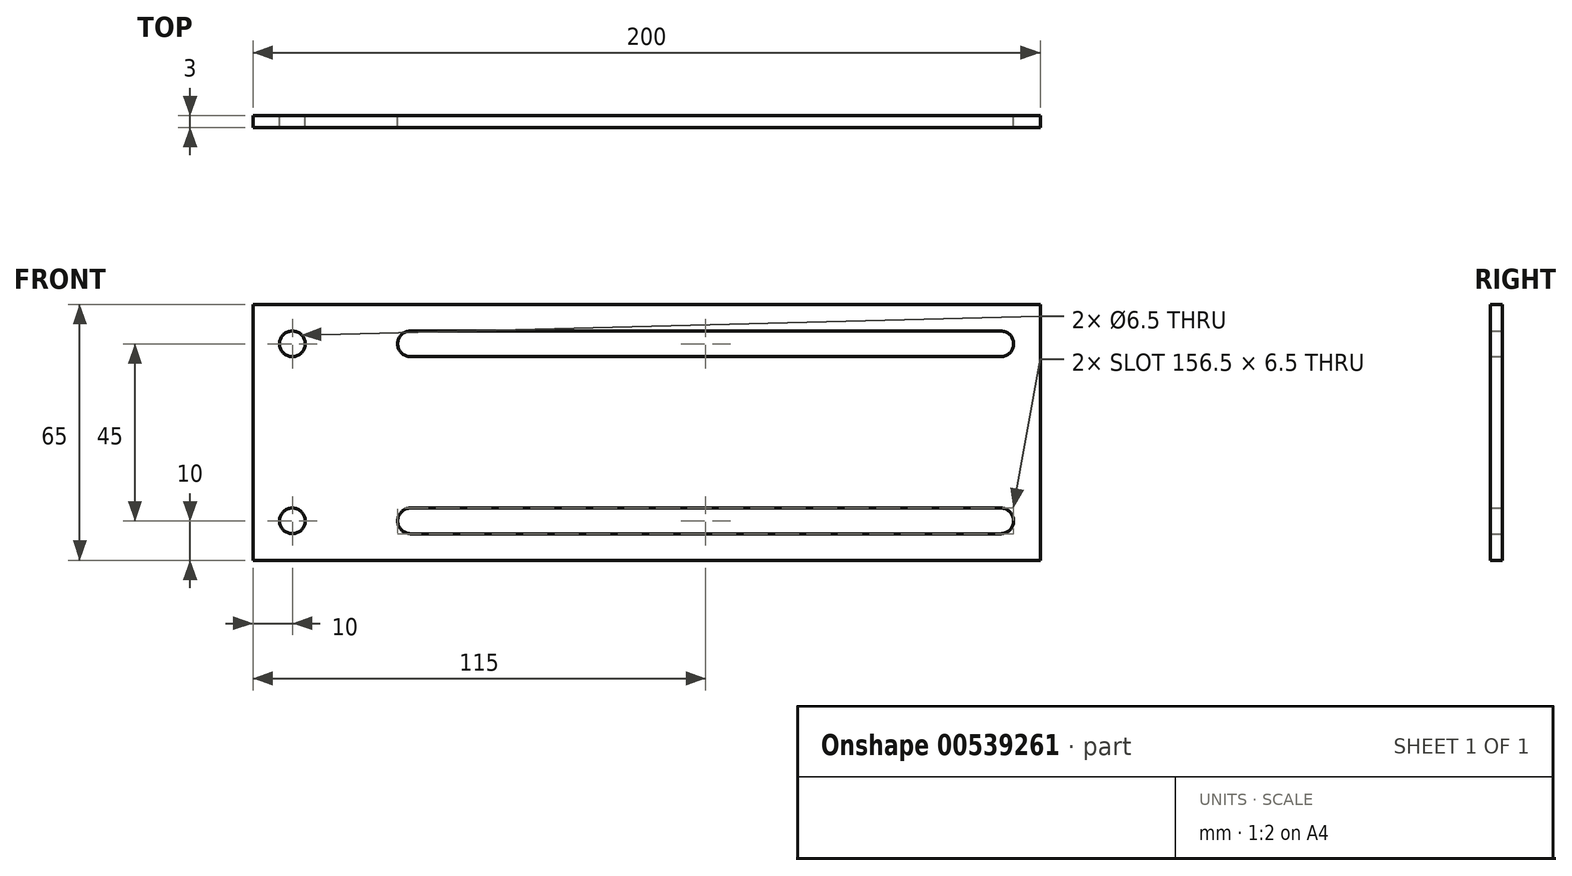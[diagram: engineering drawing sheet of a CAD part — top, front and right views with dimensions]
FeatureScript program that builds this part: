
annotation { "Feature Type Name" : "Feature", "Feature Type Description" : "" }
export const myFeature = defineFeature(function(context is Context, id is Id, definition is map)
    precondition{}
    {
        {
            var Q0;
            Q0=qCreatedBy(makeId("Front.planeOp"),FACE);
            var sketch = newSketch(context, id + "F0", { "sketchPlane" : qUnion([Q0])});
            skLineSegment(sketch, "E0.bottom", {"start": v(0, 0) * mm, "end": v(200, 0) * mm});
            skLineSegment(sketch, "E0.top", {"start": v(0, 65) * mm, "end": v(200, 65) * mm});
            skLineSegment(sketch, "E0.left", {"start": v(0, 0) * mm, "end": v(0, 65) * mm});
            skLineSegment(sketch, "E0.right", {"start": v(200, 0) * mm, "end": v(200, 65) * mm});
            skLineSegment(sketch, "E1", {"start": v(0, 10) * mm, "end": v(10, 10) * mm});
            skLineSegment(sketch, "E2", {"start": v(0, 55) * mm, "end": v(10, 55) * mm});
            skCircle(sketch, "E3", {"center": v(10, 55) * mm, "radius": 3.25 * mm});
            skCircle(sketch, "E4", {"center": v(10, 10) * mm, "radius": 3.25 * mm});
            skLineSegment(sketch, "E5", {"start": v(100, 65) * mm, "end": v(100, 0) * mm});
            skLineSegment(sketch, "E6", {"start": v(0, 32.5) * mm, "end": v(200, 32.5) * mm});
            skLineSegment(sketch, "E7", {"start": v(30, 32.5) * mm, "end": v(30, 0) * mm});
            skLineSegment(sketch, "E8.MirrorCS", {"start": v(100, 0) * mm, "end": v(100, 65) * mm});
            skLineSegment(sketch, "E9", {"start": v(10, 10) * mm, "end": v(40, 10) * mm});
            skCircle(sketch, "E10", {"center": v(40, 10) * mm, "radius": 3.25 * mm});
            skCircle(sketch, "E11.MirrorC", {"center": v(190, 10) * mm, "radius": 3.25 * mm});
            skLineSegment(sketch, "E12", {"start": v(40, 10) * mm, "end": v(40, 6.75) * mm});
            skLineSegment(sketch, "E13", {"start": v(40, 10) * mm, "end": v(40, 13.25) * mm});
            skLineSegment(sketch, "E14", {"start": v(190, 10) * mm, "end": v(190, 13.25) * mm});
            skLineSegment(sketch, "E15", {"start": v(190, 10) * mm, "end": v(190, 6.75) * mm});
            skLineSegment(sketch, "E16", {"start": v(190, 13.25) * mm, "end": v(40, 13.25) * mm});
            skLineSegment(sketch, "E17", {"start": v(40, 6.75) * mm, "end": v(190, 6.75) * mm});
            skLineSegment(sketch, "E18.MirrorCS", {"start": v(40, 55) * mm, "end": v(40, 58.25) * mm});
            skLineSegment(sketch, "E19.MirrorCS", {"start": v(190, 55) * mm, "end": v(190, 51.75) * mm});
            skLineSegment(sketch, "E20.MirrorCS", {"start": v(190, 55) * mm, "end": v(190, 58.25) * mm});
            skLineSegment(sketch, "E21.MirrorCS", {"start": v(40, 55) * mm, "end": v(40, 51.75) * mm});
            skLineSegment(sketch, "E22.MirrorCS", {"start": v(10, 55) * mm, "end": v(40, 55) * mm});
            skLineSegment(sketch, "E23.MirrorCS", {"start": v(40, 58.25) * mm, "end": v(190, 58.25) * mm});
            skCircle(sketch, "E24.MirrorC", {"center": v(190, 55) * mm, "radius": 3.25 * mm});
            skLineSegment(sketch, "E25.MirrorCS", {"start": v(190, 51.75) * mm, "end": v(40, 51.75) * mm});
            skCircle(sketch, "E26.MirrorC", {"center": v(40, 55) * mm, "radius": 3.25 * mm});
            skSolve(sketch);
        }
        {
            var Q0;
            Q0=makeQuery(id+"F0.imprint","IMPRINT",FACE,{"disambiguationData":[TD([[makeQuery(id+"F0.imprint","IMPRINT",EDGE,{"derivedFrom":sQuery(id+"F0.wireOp",EDGE,"E3")}),-1.0]])]});
            var Q1;
            Q1=makeQuery(id+"F0.imprint","IMPRINT",FACE,{"disambiguationData":[TD([[makeQuery(id+"F0.imprint","IMPRINT",EDGE,{"derivedFrom":sQuery(id+"F0.wireOp",EDGE,"94dded7e-ffbe-4f53-a43a-50ec608be8390.MirrorC")}),1.0]])]});
            var Q2;
            Q2=makeQuery(id+"F0.imprint","IMPRINT",FACE,{"disambiguationData":[TD([[makeQuery(id+"F0.imprint","IMPRINT",EDGE,{"derivedFrom":sQuery(id+"F0.wireOp",EDGE,"725528f7-230d-490f-96c3-0352711715200.MirrorC")}),1.0]])]});
            var Q3;
            {var subQ5=sQuery(id+"F0.wireOp",EDGE,"NzWXYV9I-SoYN-Hgyj-b80R-Zs6ElDGVtiVE");Q3=makeQuery(id+"F0.imprint","IMPRINT",FACE,{"disambiguationData":[TD([[makeQuery(id+"F0.imprint","IMPRINT",EDGE,{"derivedFrom":subQ5}),-1.0]])]});}
            var Q4;
            Q4=makeQuery(id+"F0.imprint","IMPRINT",FACE,{"disambiguationData":[TD([[makeQuery(id+"F0.imprint","IMPRINT",EDGE,{"derivedFrom":sQuery(id+"F0.wireOp",EDGE,"E4")}),-1.0]])]});
            var Q5;
            {var subQ3=sQuery(id+"F0.wireOp",EDGE,"7quVdxcI-sNya-2Ci5-n9LF-zZTYmZusP7LA");Q5=makeQuery(id+"F0.imprint","IMPRINT",FACE,{"disambiguationData":[TD([[makeQuery(id+"F0.imprint","IMPRINT",EDGE,{"derivedFrom":subQ3}),1.0]])]});}
            var Q6;
            {var subQ1=sQuery(id+"F0.wireOp",EDGE,"E0.left");var subQ5=sQuery(id+"F0.wireOp",EDGE,"E2");var subQ13=makeQuery(id+"F0.imprint","INTERSECT",VERTEX,{"derivedFrom":[subQ1,subQ5]});Q6=makeQuery(id+"F0.imprint","IMPRINT",FACE,{"disambiguationData":[TD([[makeQuery(id+"F0.imprint","IMPRINT",EDGE,{"disambiguationData":[TD([[subQ13,1.0]])],"derivedFrom":subQ1}),-1.0]])]});}
            var Q7;
            {var subQ5=sQuery(id+"F0.wireOp",EDGE,"E7");var subQ7=sQuery(id+"F0.wireOp",EDGE,"E6");var subQ8=makeQuery(id+"F0.imprint","INTERSECT",VERTEX,{"derivedFrom":[subQ7,subQ5]});Q7=makeQuery(id+"F0.imprint","IMPRINT",FACE,{"disambiguationData":[TD([[makeQuery(id+"F0.imprint","IMPRINT",EDGE,{"disambiguationData":[TD([[subQ8,-1.0]])],"derivedFrom":subQ7}),-1.0]])]});}
            var Q8;
            {var subQ5=sQuery(id+"F0.wireOp",EDGE,"E7");var subQ6=sQuery(id+"F0.wireOp",EDGE,"E0.bottom");var subQ7=makeQuery(id+"F0.imprint","INTERSECT",VERTEX,{"derivedFrom":[subQ6,subQ5]});Q8=makeQuery(id+"F0.imprint","IMPRINT",FACE,{"disambiguationData":[TD([[makeQuery(id+"F0.imprint","IMPRINT",EDGE,{"disambiguationData":[TD([[subQ7,-1.0]])],"derivedFrom":subQ6}),1.0]])]});}
            var Q9;
            {var subQ1=sQuery(id+"F0.wireOp",EDGE,"E0.right");var subQ5=sQuery(id+"F0.wireOp",EDGE,"E0.top");var subQ6=makeQuery(id+"F0.imprint","INTERSECT",VERTEX,{"derivedFrom":[subQ5,subQ1]});Q9=makeQuery(id+"F0.imprint","IMPRINT",FACE,{"disambiguationData":[TD([[makeQuery(id+"F0.imprint","IMPRINT",EDGE,{"disambiguationData":[TD([[subQ6,1.0]])],"derivedFrom":subQ5}),-1.0]])]});}
            var Q10;
            {var subQ5=sQuery(id+"F0.wireOp",EDGE,"E0.right");var subQ6=sQuery(id+"F0.wireOp",EDGE,"E0.bottom");var subQ7=makeQuery(id+"F0.imprint","INTERSECT",VERTEX,{"derivedFrom":[subQ6,subQ5]});Q10=makeQuery(id+"F0.imprint","IMPRINT",FACE,{"disambiguationData":[TD([[makeQuery(id+"F0.imprint","IMPRINT",EDGE,{"disambiguationData":[TD([[subQ7,1.0]])],"derivedFrom":subQ6}),1.0]])]});}
            extrude(context, id + "F1", {"entities" : qUnion([Q0, Q1, Q2, Q3, Q4, Q5, Q6, Q7, Q8, Q9, Q10]), "depth" : 3 * mm, "offsetDistance" : 25 * mm});
        }
    });
